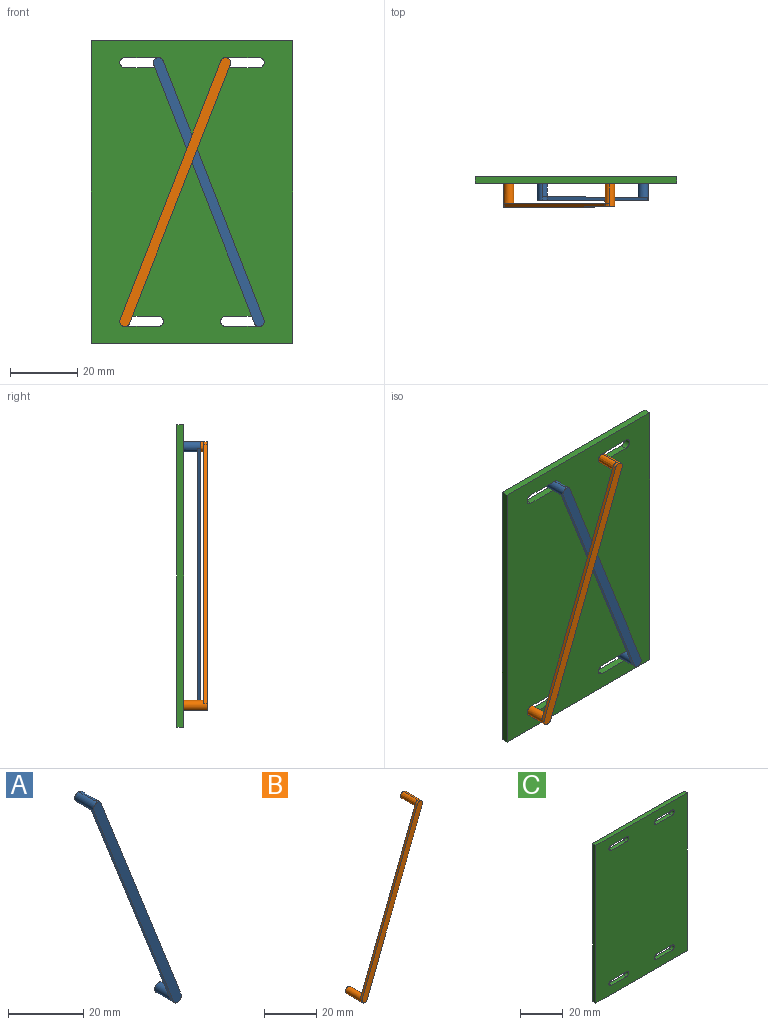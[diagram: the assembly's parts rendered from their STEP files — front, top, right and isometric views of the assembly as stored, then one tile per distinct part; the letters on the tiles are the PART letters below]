
ASSEMBLY  parts=3 mates=4
PART A: 10 faces, bbox 33x7x80 mm
  f0: cylinder r=1.5mm len=7mm, axis (0,1,0), area 31.2mm2, adj f1,f2,f3,f7,f8,f9
  f1: extruded ~6x3mm, area 28.3mm2, adj f0,f2,f3,f7
  f2: plane 3x3mm, normal (0,1,0), area 7.1mm2, adj f0,f1
  f3: plane 78.09x32.8mm, normal (0,1,0), area 240.8mm2, adj f0,f1,f4,f6,f8
  f4: cylinder r=1.5mm len=7mm, axis (0,1,0), area 61.3mm2, adj f3,f5,f6,f8,f9
  f5: plane 3x3mm, normal (0,1,0), area 7.1mm2, adj f4
  f6: plane 77x30mm, normal (0.93,0,0.36), area 82.6mm2, adj f3,f4,f7,f9
  f7: extruded ~1.4x1mm, area 1.8mm2, adj f0,f1,f6,f9
  f8: plane 77x30mm, normal (-0.93,0,-0.36), area 82.6mm2, adj f0,f3,f4,f9
  f9: plane 80x33mm, normal (0,-1,0), area 255mm2, adj f0,f4,f6,f7,f8
PART B: 10 faces, bbox 33x9x80 mm
  f0: extruded ~8x3mm, area 37.7mm2, adj f1,f2,f6,f9
  f1: cylinder r=1.5mm len=9mm, axis (0,1,0), area 40.6mm2, adj f0,f2,f5,f6,f8,f9
  f2: plane 3x3mm, normal (0,1,0), area 7.1mm2, adj f0,f1
  f3: cylinder r=1.5mm len=9mm, axis (0,1,0), area 80.1mm2, adj f4,f5,f7,f8,f9
  f4: plane 3x3mm, normal (0,1,0), area 7.1mm2, adj f3
  f5: plane 77x30mm, normal (0.93,0,-0.36), area 82.6mm2, adj f1,f3,f8,f9
  f6: extruded ~1.4x1mm, area 1.8mm2, adj f0,f1,f7,f8
  f7: plane 77x30mm, normal (-0.93,0,0.36), area 82.6mm2, adj f3,f6,f8,f9
  f8: plane 80x33mm, normal (0,-1,0), area 255mm2, adj f1,f3,f5,f6,f7
  f9: plane 78.09x32.8mm, normal (0,1,0), area 240.8mm2, adj f0,f1,f3,f5,f7
PART C: 22 faces, bbox 60x2x90 mm
  f0: plane 60x2mm, normal (0,0,-1), area 120mm2, adj f1,f19,f20,f21
  f1: plane 90x2mm, normal (1,0,0), area 180mm2, adj f0,f2,f20,f21
  f2: plane 60x2mm, normal (0,0,1), area 120mm2, adj f1,f19,f20,f21
  f3: cylinder r=1.5mm len=3mm, axis (0,1,0), area 9.4mm2, adj f4,f15,f20,f21
  f4: plane 10x2mm, normal (0,0,-1), area 20mm2, adj f3,f5,f20,f21
  f5: cylinder r=1.5mm len=3mm, axis (0,1,0), area 9.4mm2, adj f4,f15,f20,f21
  f6: cylinder r=1.5mm len=3mm, axis (0,1,0), area 9.4mm2, adj f7,f16,f20,f21
  f7: plane 10x2mm, normal (0,0,-1), area 20mm2, adj f6,f8,f20,f21
  f8: cylinder r=1.5mm len=3mm, axis (0,1,0), area 9.4mm2, adj f7,f16,f20,f21
  f9: plane 10x2mm, normal (0,0,1), area 20mm2, adj f10,f17,f20,f21
  f10: cylinder r=1.5mm len=3mm, axis (0,1,0), area 9.4mm2, adj f9,f11,f20,f21
  f11: plane 10x2mm, normal (0,0,-1), area 20mm2, adj f10,f17,f20,f21
  f12: plane 10x2mm, normal (0,0,1), area 20mm2, adj f13,f18,f20,f21
  f13: cylinder r=1.5mm len=3mm, axis (0,1,0), area 9.4mm2, adj f12,f14,f20,f21
  f14: plane 10x2mm, normal (0,0,-1), area 20mm2, adj f13,f18,f20,f21
  f15: plane 10x2mm, normal (0,0,1), area 20mm2, adj f3,f5,f20,f21
  f16: plane 10x2mm, normal (0,0,1), area 20mm2, adj f6,f8,f20,f21
  f17: cylinder r=1.5mm len=3mm, axis (0,1,0), area 9.4mm2, adj f9,f11,f20,f21
  f18: cylinder r=1.5mm len=3mm, axis (0,1,0), area 9.4mm2, adj f12,f14,f20,f21
  f19: plane 90x2mm, normal (-1,0,0), area 180mm2, adj f0,f2,f20,f21
  f20: plane 90x60mm, normal (0,-1,0), area 5251.7mm2, adj f0,f1,f2,f3,f4,f5,f6,f7
  f21: plane 90x60mm, normal (0,1,0), area 5251.7mm2, adj f0,f1,f2,f3,f4,f5,f6,f7
PLACE A t=(10,-3,0)mm
PLACE B t=(-10,-3,0)mm
PLACE C at identity fixed
MATE pin_slot B.f1 <-> C.f21  axis (0,1,0) through (10,0,38.5)mm
MATE pin_slot B.f3 <-> C.f10  axis (0,1,0) through (-20,0,-38.5)mm
MATE pin_slot C.f21 <-> A.f4  axis (0,1,0) through (15,0,-38.5)mm
MATE pin_slot A.f0 <-> C.f21  axis (0,1,0) through (-10,0,38.5)mm
